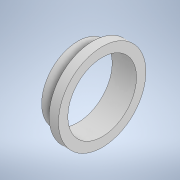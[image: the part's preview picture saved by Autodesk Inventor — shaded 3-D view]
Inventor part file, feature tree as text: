
AUTODESK INVENTOR PART (.ipt)
format: ipt  version: 2020 (Build 240168000, 168)  size: 118,784 bytes
history: native  units: mm
features: revolve x1, sketch x1
ambient origin geometry x8: Origin, YZ Plane, XZ Plane, XY Plane, X Axis, Y Axis, Z Axis, Center Point
bodies: 实体1 (feature_tree)
feature tree (2):
  revolve  "旋转1"  [1 undecoded]
  sketch  "草图1"  dims[d0=140.0mm d1=110.0mm d2=39.0mm d3=15.0mm d4=116.0mm d5=90.0deg]
note: 1 required parameter value undecoded (feature->parameter linkage not recoverable at this tier; creation-order binding heuristic only, values carry confidence <= 0.55)
